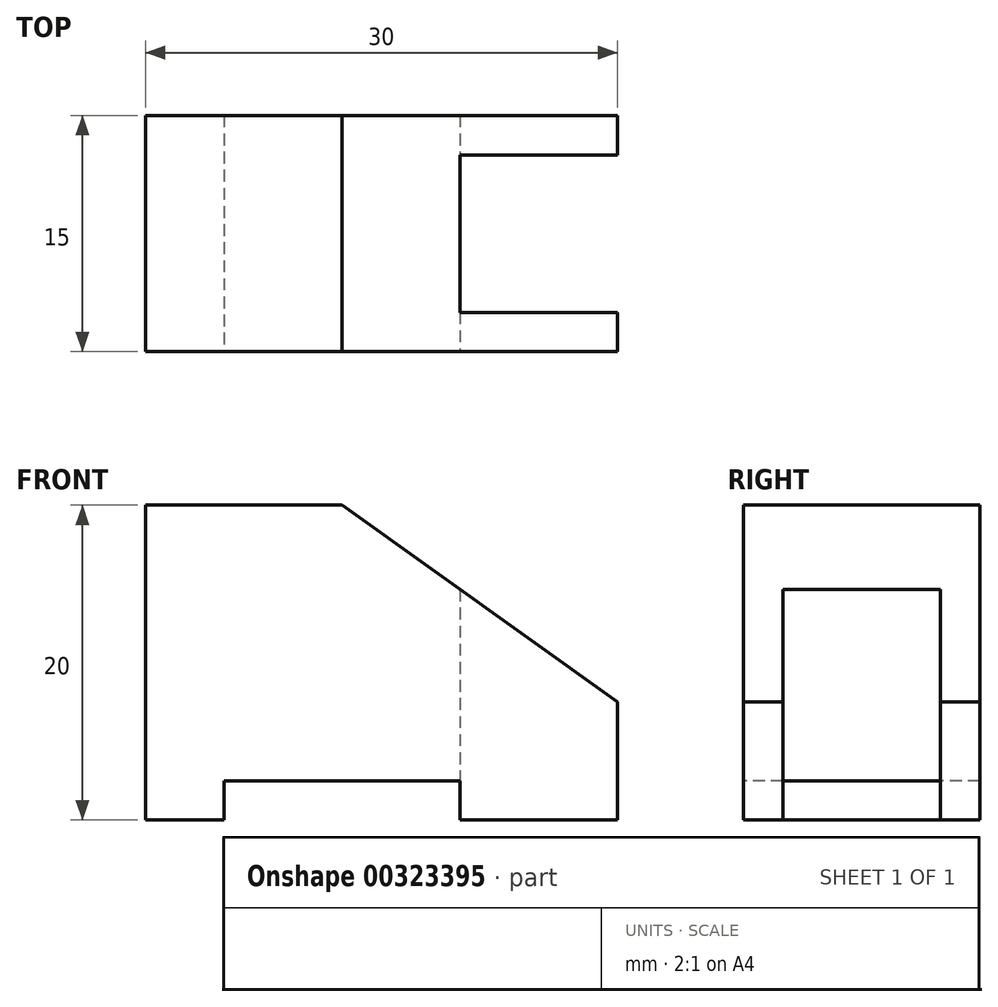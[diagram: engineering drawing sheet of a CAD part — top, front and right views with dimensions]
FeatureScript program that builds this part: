
annotation { "Feature Type Name" : "Feature", "Feature Type Description" : "" }
export const myFeature = defineFeature(function(context is Context, id is Id, definition is map)
    precondition{}
    {
        {
            var Q0;
            Q0=qCreatedBy(makeId("Top.planeOp"),FACE);
            var sketch = newSketch(context, id + "F0", { "sketchPlane" : qUnion([Q0])});
            skLineSegment(sketch, "E0", {"start": v(0, 0) * mm, "end": v(0, 15) * mm});
            skLineSegment(sketch, "E1", {"start": v(0, 15) * mm, "end": v(12.5, 15) * mm});
            skLineSegment(sketch, "E2", {"start": v(12.5, 15) * mm, "end": v(12.5, 0) * mm});
            skLineSegment(sketch, "E3", {"start": v(12.5, 0) * mm, "end": v(0, 0) * mm});
            skLineSegment(sketch, "E4", {"start": v(12.5, 15) * mm, "end": v(30, 15) * mm});
            skLineSegment(sketch, "E5", {"start": v(30, 15) * mm, "end": v(30, 12.5) * mm});
            skLineSegment(sketch, "E6", {"start": v(30, 12.5) * mm, "end": v(20, 12.5) * mm});
            skLineSegment(sketch, "E7", {"start": v(20, 12.5) * mm, "end": v(20, 2.5) * mm});
            skLineSegment(sketch, "E8", {"start": v(20, 2.5) * mm, "end": v(30, 2.5) * mm});
            skLineSegment(sketch, "E9", {"start": v(30, 2.5) * mm, "end": v(30, 0) * mm});
            skLineSegment(sketch, "E10", {"start": v(30, 0) * mm, "end": v(12.5, 0) * mm});
            skSolve(sketch);
        }
        {
            var Q0;
            Q0 = qSketchRegion(id + "F0", true);
            extrude(context, id + "F1", {"entities" : qUnion([Q0]), "depth" : 20 * mm});
        }
        {
            var Q0;
            Q0=makeQuery(id+"F1.opExtrude","SWEPT_FACE",FACE,{"disambiguationData":[OSD([sQuery(id+"F0.wireOp",EDGE,"E3"),sQuery(id+"F0.wireOp",EDGE,"E10")])]});
            var sketch = newSketch(context, id + "F2", { "sketchPlane" : qUnion([Q0])});
            skLineSegment(sketch, "E11", {"start": v(0, 20) * mm, "end": v(30, 20) * mm});
            skLineSegment(sketch, "E12", {"start": v(30, 20) * mm, "end": v(30, 0) * mm});
            skLineSegment(sketch, "E13", {"start": v(30, 0) * mm, "end": v(0, 0) * mm});
            skLineSegment(sketch, "E14", {"start": v(0, 0) * mm, "end": v(0, 20) * mm});
            skLineSegment(sketch, "E15", {"start": v(5, 0) * mm, "end": v(5, 2.5) * mm});
            skLineSegment(sketch, "E16", {"start": v(5, 2.5) * mm, "end": v(20, 2.5) * mm});
            skLineSegment(sketch, "E17", {"start": v(20, 2.5) * mm, "end": v(20, 0) * mm});
            skLineSegment(sketch, "E18", {"start": v(12.5, 20) * mm, "end": v(30, 7.5) * mm});
            skSolve(sketch);
        }
        {
            var Q0;
            {var subQ0=sQuery(id+"F2.wireOp",EDGE,"E15");Q0=makeQuery(id+"F2.imprint","IMPRINT",FACE,{"disambiguationData":[TD([[makeQuery(id+"F2.imprint","IMPRINT",EDGE,{"derivedFrom":subQ0}),-1.0]])]});}
            var Q1;
            {var subQ3=sQuery(id+"F2.wireOp",EDGE,"E18");Q1=makeQuery(id+"F2.imprint","IMPRINT",FACE,{"disambiguationData":[TD([[makeQuery(id+"F2.imprint","IMPRINT",EDGE,{"derivedFrom":subQ3}),1.0]])]});}
            extrude(context, id + "F3", {"entities" : qUnion([Q0, Q1]), "operationType" : NewBodyOperationType.REMOVE, "endBound" : BoundingType.THROUGH_ALL, "oppositeDirection" : true, "depth" : 25 * mm});
        }
    });
